# Revit family: QF_ELECTROLUXPROFESSIONAL_CC0FW0_EDR150EC6MV
name_source: partatom
category: Specialty Equipment
revit_build: Autodesk Revit 2018 (Build: 20190510_1515(x64)
units: mm (PartAtom-declared; Revit-internal decimal feet)

## family parameters
Always vertical = Yes
Cut with Voids When Loaded = No
Part Type = Normal
Room Calculation Point = No
Round Connector Dimension = Use Diameter
Shared = No
Work Plane-Based = No

## types (2) — shared parameters
Accessory = Yes
Cold Water Size = 0 mm
Compressed Air Pressure = 0.0 Pa
Compressed Air Size = 0 mm
Compressed Air Volume = 0.0 L/s
Condensate Return Size = 0 mm
Cycle = 0 Hz
Gas Input Pressure = 0
Gas Size = 0 mm
Hot Water Size = 0 mm
Refrigerant Compressor Remote = Yes
Refrigeration Liquid Line Size = 0 mm
Refrigeration Suction Line Size = 0 mm
Steam Supply Maximum Pressure = 0.0 Pa
Steam Supply Minimum Pressure = 0.0 Pa
Steam Supply Size = 0 mm
Volts = 0 V
Watts = 0 W
Weight = 0.00 kg
zero-valued in all types: Depth Actual, Gas KW, Height Actual, Length Actual, Phase, Steam Pounds per Hour

## type names (no varying parameters)
- EDR150EC5MV
- Standard

note: source unit labels omitted for Gas Input Pressure — the stored unit's dimension contradicts the parameter name (converter mislabeling)

## geometry (parser evidence)
native form markers: Sweep x5
no freeform markers — native parametric forms only
